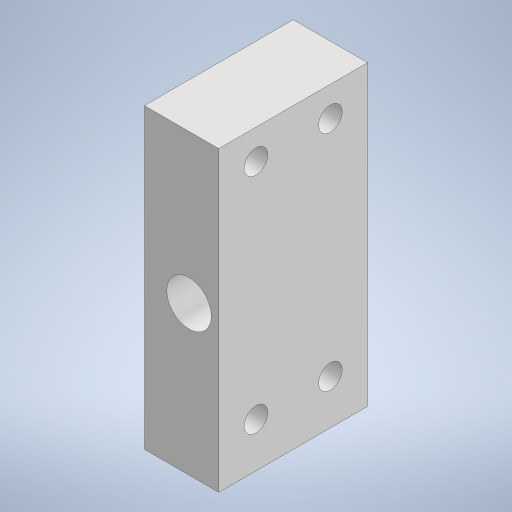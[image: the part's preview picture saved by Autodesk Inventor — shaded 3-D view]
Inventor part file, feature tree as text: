
AUTODESK INVENTOR PART (.ipt)
format: ipt  version: 2024.1 (Build 281209000, 209)  size: 237,568 bytes
history: native  units: in
note: dims shown in document units (in); Inventor stores cm internally (conversion verified against a paired STEP export)
features: extrude x3, sketch x3
ambient origin geometry x8: Origin, YZ Plane, XZ Plane, XY Plane, X Axis, Y Axis, Z Axis, Center Point
bodies: Solid1 (feature_tree)
feature tree (6):
  extrude  "Extrusion1"  Depth=0.3937in
  extrude  "Extrusion2"  Depth=0.1969in
  extrude  "Extrusion3"  Depth=0.3937in
  sketch  "Sketch1"  dims[d0=0.7874in d1=0.3937in]
  sketch  "Sketch2"  dims[d2=0.1969in d3=0.0in d4=0.1181in]
  sketch  "Sketch3"  dims[d5=0.0787in d6=0.3937in d7=0.0in d8=0.0in d9=0.063in d11=0.063in d12=0.063in d13=0.063in d14=0.0984in d15=0.0984in d16=0.1181in d17=0.1181in d18=0.5906in d19=0.5906in d20=0.0984in d21=0.0984in d22=0.0in d23=0.0in]
